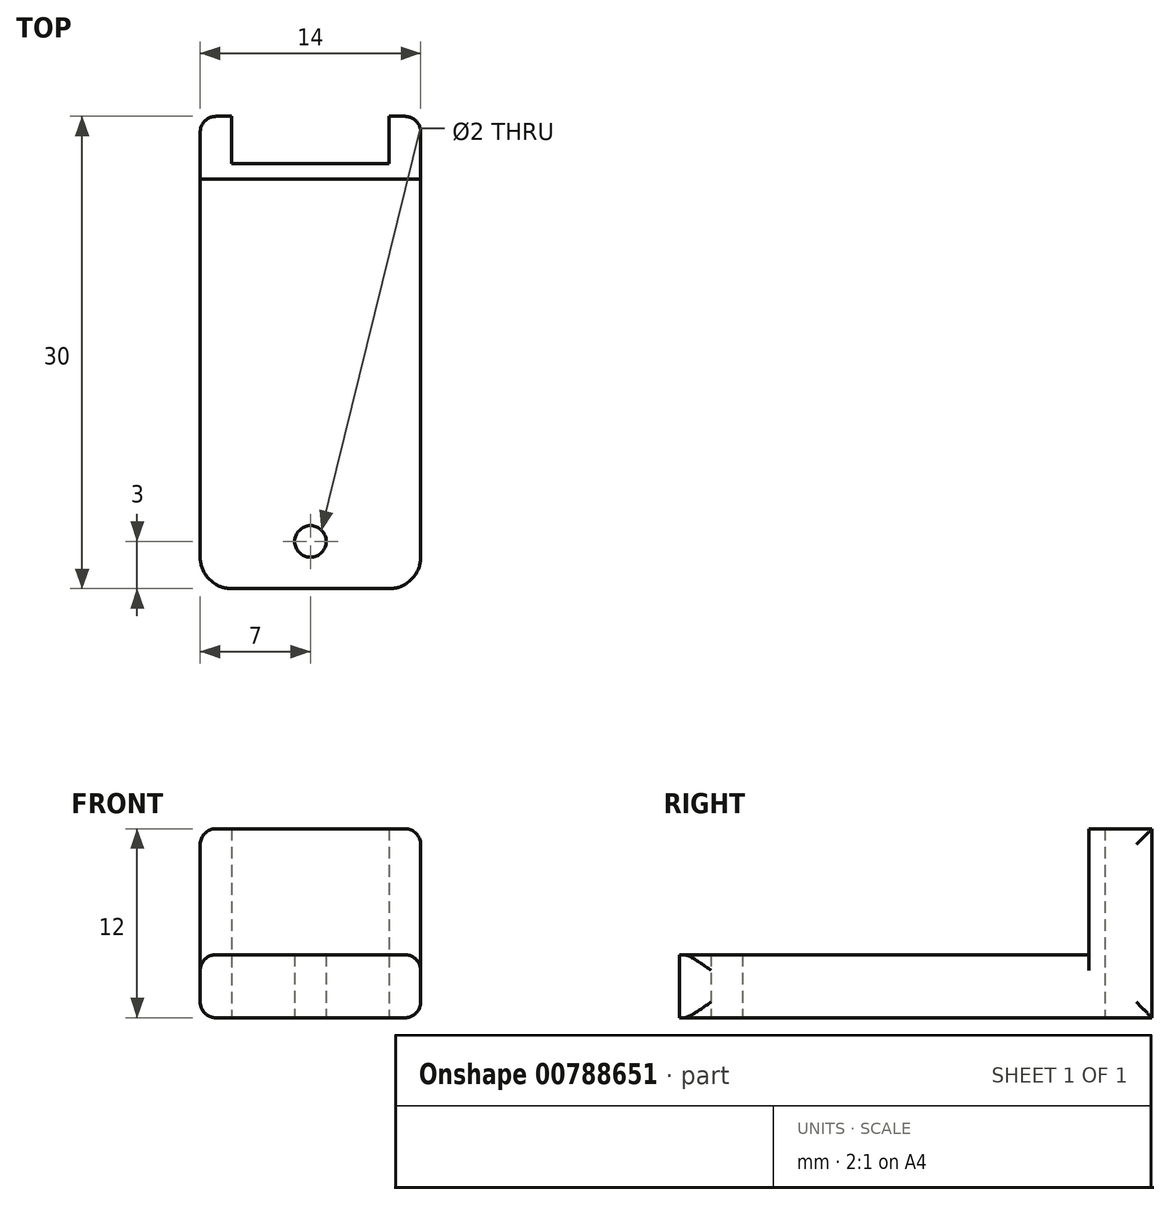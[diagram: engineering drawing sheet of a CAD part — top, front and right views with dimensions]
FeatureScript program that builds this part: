
annotation { "Feature Type Name" : "Feature", "Feature Type Description" : "" }
export const myFeature = defineFeature(function(context is Context, id is Id, definition is map)
    precondition{}
    {
        {
            var Q0;
            Q0=qCreatedBy(makeId("Top.planeOp"),FACE);
            var sketch = newSketch(context, id + "F0", { "sketchPlane" : qUnion([Q0])});
            skCircle(sketch, "E0", {"center": v(0, 3) * mm, "radius": 1 * mm});
            skLineSegment(sketch, "E1.bottom", {"start": v(-7, 0) * mm, "end": v(7, 0) * mm});
            skLineSegment(sketch, "E1.top", {"start": v(-7, 30) * mm, "end": v(7, 30) * mm});
            skLineSegment(sketch, "E1.left", {"start": v(-7, 0) * mm, "end": v(-7, 30) * mm});
            skLineSegment(sketch, "E1.right", {"start": v(7, 0) * mm, "end": v(7, 30) * mm});
            skSolve(sketch);
        }
        {
            var Q0;
            Q0=makeQuery(id+"F0.imprint","IMPRINT",FACE,{"disambiguationData":[TD([[makeQuery(id+"F0.imprint","IMPRINT",EDGE,{"derivedFrom":sQuery(id+"F0.wireOp",EDGE,"E0")}),-1.0]])]});
            extrude(context, id + "F1", {"entities" : qUnion([Q0]), "depth" : 4 * mm, "offsetDistance" : 25 * mm});
        }
        {
            var Q0;
            Q0=makeQuery(id+"F1.opExtrude","CAP_FACE",FACE,{"disambiguationData":[OSD([sQuery(id+"F0.wireOp",EDGE,"E0"),sQuery(id+"F0.wireOp",EDGE,"E1.bottom"),sQuery(id+"F0.wireOp",EDGE,"E1.top"),sQuery(id+"F0.wireOp",EDGE,"E1.left"),sQuery(id+"F0.wireOp",EDGE,"E1.right")])],"isStart":false});
            var sketch = newSketch(context, id + "F2", { "sketchPlane" : qUnion([Q0])});
            skLineSegment(sketch, "E2.bottom", {"start": v(-5, 30) * mm, "end": v(5, 30) * mm});
            skLineSegment(sketch, "E2.top", {"start": v(-5, 27) * mm, "end": v(5, 27) * mm});
            skLineSegment(sketch, "E2.left", {"start": v(-5, 30) * mm, "end": v(-5, 27) * mm});
            skLineSegment(sketch, "E2.right", {"start": v(5, 30) * mm, "end": v(5, 27) * mm});
            skPoint(sketch, "E3", {"position": v(0, 30) * mm});
            skLineSegment(sketch, "E4", {"start": v(-7, 26) * mm, "end": v(7, 26) * mm});
            skSolve(sketch);
        }
        {
            var Q0;
            {var subQ2=sQuery(id+"F2.wireOp",EDGE,"E2.left");Q0=makeQuery(id+"F2.imprint","IMPRINT",FACE,{"disambiguationData":[TD([[makeQuery(id+"F2.imprint","IMPRINT",EDGE,{"derivedFrom":subQ2}),-1.0]])]});}
            extrude(context, id + "F3", {"entities" : qUnion([Q0]), "operationType" : NewBodyOperationType.ADD, "depth" : 8 * mm, "offsetDistance" : 25 * mm});
        }
        {
            var Q0;
            {var subQ1=sQuery(id+"F0.wireOp",EDGE,"E1.top");var subQ3=sQuery(id+"F0.wireOp",EDGE,"E1.left");var subQ6=sQuery(id+"F0.wireOp",EDGE,"E1.right");Q0=makeQuery(id+"F3.boolean.opBoolean","SPLIT",FACE,{"disambiguationData":[TD([makeQuery(id+"F1.opExtrude","SWEPT_FACE",FACE,{"disambiguationData":[OSD([subQ1])]})])],"derivedFrom":makeQuery(id+"F1.opExtrude","CAP_FACE",FACE,{"disambiguationData":[OSD([sQuery(id+"F0.wireOp",EDGE,"E0"),sQuery(id+"F0.wireOp",EDGE,"E1.bottom"),subQ1,subQ3,subQ6])],"isStart":false})});}
            extrude(context, id + "F4", {"entities" : qUnion([Q0]), "operationType" : NewBodyOperationType.REMOVE, "endBound" : BoundingType.THROUGH_ALL, "oppositeDirection" : true, "depth" : 25 * mm, "offsetDistance" : 25 * mm});
        }
        {
            var Q0;
            {var subQ0=sQuery(id+"F0.wireOp",EDGE,"E1.left");var subQ1=sQuery(id+"F0.wireOp",EDGE,"E1.top");Q0=makeQuery(id+"F3.boolean.opBoolean","MERGE",EDGE,{"derivedFrom":[makeQuery(id+"F1.opExtrude","SWEPT_EDGE",EDGE,{"disambiguationData":[OSD([subQ1,subQ0])]}),makeQuery(id+"F3.opExtrude","SWEPT_EDGE",EDGE,{"disambiguationData":[OSD([subQ1,subQ0])]})]});}
            var Q1;
            {var subQ0=sQuery(id+"F0.wireOp",EDGE,"E1.right");var subQ1=sQuery(id+"F0.wireOp",EDGE,"E1.top");Q1=makeQuery(id+"F3.boolean.opBoolean","MERGE",EDGE,{"derivedFrom":[makeQuery(id+"F1.opExtrude","SWEPT_EDGE",EDGE,{"disambiguationData":[OSD([subQ1,subQ0])]}),makeQuery(id+"F3.opExtrude","SWEPT_EDGE",EDGE,{"disambiguationData":[OSD([subQ1,subQ0])]})]});}
            var Q2;
            Q2=makeQuery(id+"F3.opExtrude","CAP_EDGE",EDGE,{"disambiguationData":[OSD([sQuery(id+"F0.wireOp",EDGE,"E1.left")])],"isStart":false});
            var Q3;
            Q3=makeQuery(id+"F3.opExtrude","CAP_EDGE",EDGE,{"disambiguationData":[OSD([sQuery(id+"F0.wireOp",EDGE,"E1.right")])],"isStart":false});
            var Q4;
            Q4=makeQuery(id+"F1.opExtrude","CAP_EDGE",EDGE,{"disambiguationData":[OSD([sQuery(id+"F0.wireOp",EDGE,"E1.right")])],"isStart":true});
            var Q5;
            Q5=makeQuery(id+"F1.opExtrude","CAP_EDGE",EDGE,{"disambiguationData":[OSD([sQuery(id+"F0.wireOp",EDGE,"E1.left")])],"isStart":true});
            var Q6;
            Q6=makeQuery(id+"F1.opExtrude","CAP_EDGE",EDGE,{"disambiguationData":[OSD([sQuery(id+"F0.wireOp",EDGE,"E1.left")])],"isStart":false});
            var Q7;
            Q7=makeQuery(id+"F1.opExtrude","CAP_EDGE",EDGE,{"disambiguationData":[OSD([sQuery(id+"F0.wireOp",EDGE,"E1.right")])],"isStart":false});
            fillet(context, id + "F5", {"entities" : qUnion([Q0, Q1, Q2, Q3, Q4, Q5, Q6, Q7]), "radius" : 1 * mm, "tangentPropagation" : true, "allowEdgeOverflow" : false});
        }
        {
            var Q0;
            Q0=makeQuery(id+"F1.opExtrude","SWEPT_EDGE",EDGE,{"disambiguationData":[OSD([sQuery(id+"F0.wireOp",EDGE,"E1.bottom"),sQuery(id+"F0.wireOp",EDGE,"E1.left")])]});
            var Q1;
            Q1=makeQuery(id+"F1.opExtrude","SWEPT_EDGE",EDGE,{"disambiguationData":[OSD([sQuery(id+"F0.wireOp",EDGE,"E1.bottom"),sQuery(id+"F0.wireOp",EDGE,"E1.right")])]});
            fillet(context, id + "F6", {"entities" : qUnion([Q0, Q1]), "radius" : 2 * mm, "allowEdgeOverflow" : false});
        }
    });
